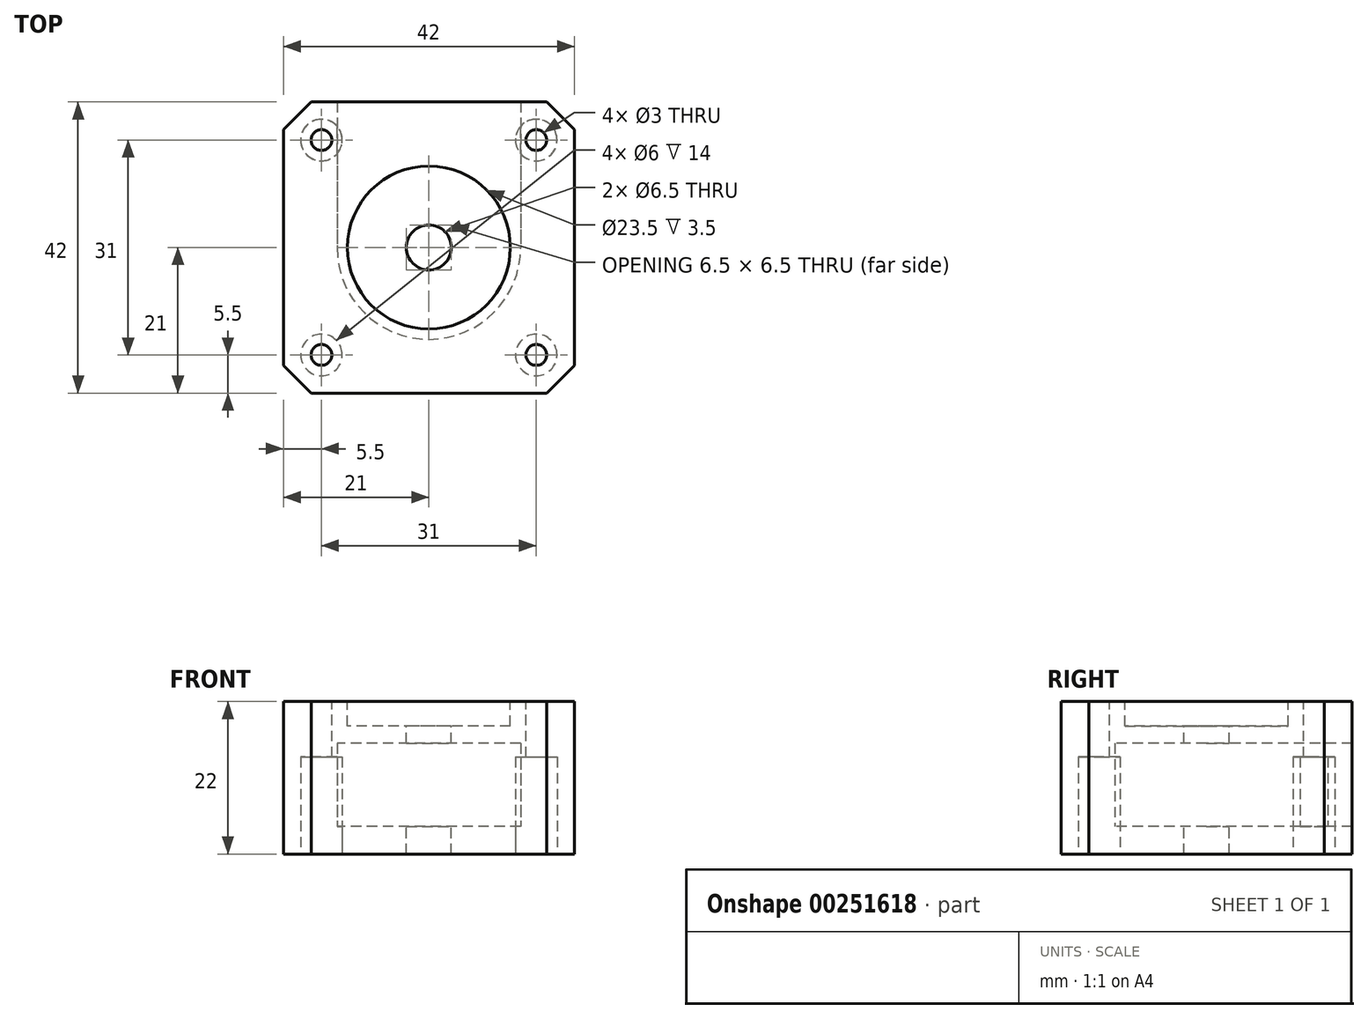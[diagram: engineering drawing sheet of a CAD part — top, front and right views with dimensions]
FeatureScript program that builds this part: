
annotation { "Feature Type Name" : "Feature", "Feature Type Description" : "" }
export const myFeature = defineFeature(function(context is Context, id is Id, definition is map)
    precondition{}
    {
        {
            var Q0;
            Q0=qCreatedBy(makeId("Top.planeOp"),FACE);
            var sketch = newSketch(context, id + "F0", { "sketchPlane" : qUnion([Q0])});
            skLineSegment(sketch, "E0.bottom", {"start": v(21, -21) * mm, "end": v(-21, -21) * mm});
            skLineSegment(sketch, "E0.top", {"start": v(21, 21) * mm, "end": v(-21, 21) * mm});
            skLineSegment(sketch, "E0.left", {"start": v(21, -21) * mm, "end": v(21, 21) * mm});
            skLineSegment(sketch, "E0.right", {"start": v(-21, -21) * mm, "end": v(-21, 21) * mm});
            skPoint(sketch, "E0.middle", {"position": v(0, 0) * mm});
            skSolve(sketch);
        }
        {
            var Q0;
            Q0 = qSketchRegion(id + "F0", true);
            extrude(context, id + "F1", {"entities" : qUnion([Q0]), "depth" : 22 * mm});
        }
        {
            var Q0;
            Q0=makeQuery(id+"F1.opExtrude","SWEPT_EDGE",EDGE,{"disambiguationData":[OSD([sQuery(id+"F0.wireOp",EDGE,"E0.bottom"),sQuery(id+"F0.wireOp",EDGE,"E0.right")])]});
            var Q1;
            Q1=makeQuery(id+"F1.opExtrude","SWEPT_EDGE",EDGE,{"disambiguationData":[OSD([sQuery(id+"F0.wireOp",EDGE,"E0.bottom"),sQuery(id+"F0.wireOp",EDGE,"E0.left")])]});
            var Q2;
            Q2=makeQuery(id+"F1.opExtrude","SWEPT_EDGE",EDGE,{"disambiguationData":[OSD([sQuery(id+"F0.wireOp",EDGE,"E0.top"),sQuery(id+"F0.wireOp",EDGE,"E0.right")])]});
            var Q3;
            Q3=makeQuery(id+"F1.opExtrude","SWEPT_EDGE",EDGE,{"disambiguationData":[OSD([sQuery(id+"F0.wireOp",EDGE,"E0.top"),sQuery(id+"F0.wireOp",EDGE,"E0.left")])]});
            chamfer(context, id + "F2", {"entities" : qUnion([Q0, Q1, Q2, Q3]), "width" : 4 * mm, "tangentPropagation" : true});
        }
        {
            var Q0;
            Q0=makeQuery(id+"F1.opExtrude","CAP_FACE",FACE,{"disambiguationData":[OSD([sQuery(id+"F0.wireOp",EDGE,"E0.bottom"),sQuery(id+"F0.wireOp",EDGE,"E0.top"),sQuery(id+"F0.wireOp",EDGE,"E0.left"),sQuery(id+"F0.wireOp",EDGE,"E0.right")])],"isStart":false});
            var sketch = newSketch(context, id + "F3", { "sketchPlane" : qUnion([Q0])});
            skCircle(sketch, "E1", {"center": v(0, 0) * mm, "radius": 11.75 * mm});
            skSolve(sketch);
        }
        {
            var Q0;
            Q0 = qSketchRegion(id + "F3", true);
            extrude(context, id + "F4", {"entities" : qUnion([Q0]), "operationType" : NewBodyOperationType.REMOVE, "oppositeDirection" : true, "depth" : 3.5 * mm});
        }
        {
            var Q0;
            Q0=makeQuery(id+"F4.boolean.opBoolean","COPY",FACE,{"derivedFrom":makeQuery(id+"F4.opExtrude","CAP_FACE",FACE,{"disambiguationData":[OSD([sQuery(id+"F3.wireOp",EDGE,"E1")])],"isStart":false})});
            var sketch = newSketch(context, id + "F5", { "sketchPlane" : qUnion([Q0])});
            skCircle(sketch, "E2", {"center": v(0, 0) * mm, "radius": 3.25 * mm});
            skSolve(sketch);
        }
        {
            var Q0;
            Q0 = qSketchRegion(id + "F5", true);
            extrude(context, id + "F6", {"entities" : qUnion([Q0]), "operationType" : NewBodyOperationType.REMOVE, "endBound" : BoundingType.THROUGH_ALL, "oppositeDirection" : true, "depth" : 25.4 * mm});
        }
        {
            var Q0;
            Q0=makeQuery(id+"F1.opExtrude","CAP_FACE",FACE,{"disambiguationData":[OSD([sQuery(id+"F0.wireOp",EDGE,"E0.bottom"),sQuery(id+"F0.wireOp",EDGE,"E0.top"),sQuery(id+"F0.wireOp",EDGE,"E0.left"),sQuery(id+"F0.wireOp",EDGE,"E0.right")])],"isStart":true});
            var sketch = newSketch(context, id + "F7", { "sketchPlane" : qUnion([Q0])});
            skLineSegment(sketch, "E3", {"start": v(-13.25, -21) * mm, "end": v(-13.25, 0) * mm});
            skLineSegment(sketch, "E4", {"start": v(13.25, -21) * mm, "end": v(13.25, 0) * mm});
            skLineSegment(sketch, "E5", {"start": v(0, -21) * mm, "end": v(0, 21) * mm, "construction": true});
            skArc(sketch, "E6", {"start": v(-13.25, 0) * mm, "mid": v(0, 13.25) * mm, "end": v(13.25, 0) * mm});
            skLineSegment(sketch, "E7", {"start": v(-13.25, -21) * mm, "end": v(13.25, -21) * mm});
            skSolve(sketch);
        }
        {
            var Q0;
            Q0 = qSketchRegion(id + "F7", true);
            extrude(context, id + "F8", {"entities" : qUnion([Q0]), "operationType" : NewBodyOperationType.REMOVE, "oppositeDirection" : true, "depth" : 16 * mm, "hasSecondDirection" : true, "secondDirectionOppositeDirection" : true, "secondDirectionDepth" : 4 * mm});
        }
        {
            var Q0;
            Q0=makeQuery(id+"F1.opExtrude","CAP_FACE",FACE,{"disambiguationData":[OSD([sQuery(id+"F0.wireOp",EDGE,"E0.bottom"),sQuery(id+"F0.wireOp",EDGE,"E0.top"),sQuery(id+"F0.wireOp",EDGE,"E0.left"),sQuery(id+"F0.wireOp",EDGE,"E0.right")])],"isStart":false});
            var sketch = newSketch(context, id + "F9", { "sketchPlane" : qUnion([Q0])});
            skLineSegment(sketch, "E8.bottom", {"start": v(15.5, -15.5) * mm, "end": v(-15.5, -15.5) * mm, "construction": true});
            skLineSegment(sketch, "E8.top", {"start": v(15.5, 15.5) * mm, "end": v(-15.5, 15.5) * mm, "construction": true});
            skLineSegment(sketch, "E8.left", {"start": v(15.5, -15.5) * mm, "end": v(15.5, 15.5) * mm, "construction": true});
            skLineSegment(sketch, "E8.right", {"start": v(-15.5, -15.5) * mm, "end": v(-15.5, 15.5) * mm, "construction": true});
            skPoint(sketch, "E8.middle", {"position": v(0, 0) * mm});
            skCircle(sketch, "E9", {"center": v(-15.5, 15.5) * mm, "radius": 1.5 * mm});
            skCircle(sketch, "E10", {"center": v(15.5, 15.5) * mm, "radius": 1.5 * mm});
            skCircle(sketch, "E11", {"center": v(-15.5, -15.5) * mm, "radius": 1.5 * mm});
            skCircle(sketch, "E12", {"center": v(15.5, -15.5) * mm, "radius": 1.5 * mm});
            skSolve(sketch);
        }
        {
            var Q0;
            Q0 = qSketchRegion(id + "F9", true);
            extrude(context, id + "F10", {"entities" : qUnion([Q0]), "operationType" : NewBodyOperationType.REMOVE, "endBound" : BoundingType.THROUGH_ALL, "oppositeDirection" : true, "depth" : 25.4 * mm});
        }
        {
            var Q0;
            Q0=makeQuery(id+"F1.opExtrude","CAP_FACE",FACE,{"disambiguationData":[OSD([sQuery(id+"F0.wireOp",EDGE,"E0.bottom"),sQuery(id+"F0.wireOp",EDGE,"E0.top"),sQuery(id+"F0.wireOp",EDGE,"E0.left"),sQuery(id+"F0.wireOp",EDGE,"E0.right")])],"isStart":true});
            var sketch = newSketch(context, id + "F11", { "sketchPlane" : qUnion([Q0])});
            skCircle(sketch, "E13", {"center": v(-15.5, 15.5) * mm, "radius": 3 * mm});
            skCircle(sketch, "E14", {"center": v(15.5, 15.5) * mm, "radius": 3 * mm});
            skCircle(sketch, "E15", {"center": v(-15.5, -15.5) * mm, "radius": 3 * mm});
            skCircle(sketch, "E16", {"center": v(15.5, -15.5) * mm, "radius": 3 * mm});
            skSolve(sketch);
        }
        {
            var Q0;
            Q0 = qSketchRegion(id + "F11", true);
            extrude(context, id + "F12", {"entities" : qUnion([Q0]), "operationType" : NewBodyOperationType.REMOVE, "oppositeDirection" : true, "depth" : 14 * mm});
        }
    });
